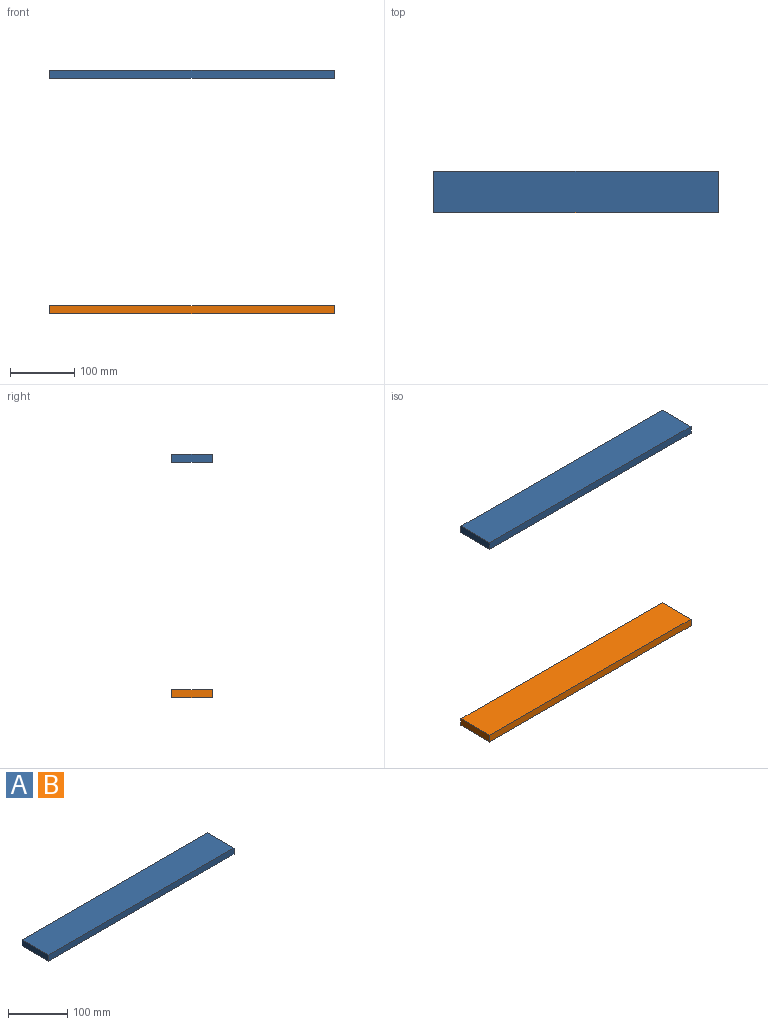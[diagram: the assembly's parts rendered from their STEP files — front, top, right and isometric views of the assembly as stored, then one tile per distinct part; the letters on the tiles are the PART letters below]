
ASSEMBLY  parts=2 mates=1
PART A: 6 faces, bbox 444.5x63.5x12.7 mm
  f0: plane 63.5x12.7mm, normal (1,0,0), area 806.5mm2, adj f1,f3,f4,f5
  f1: plane 444.5x12.7mm, normal (0,1,0), area 5645.2mm2, adj f0,f2,f4,f5
  f2: plane 63.5x12.7mm, normal (-1,0,0), area 806.5mm2, adj f1,f3,f4,f5
  f3: plane 444.5x12.7mm, normal (0,-1,0), area 5645.2mm2, adj f0,f2,f4,f5
  f4: plane 444.5x63.5mm, normal (0,0,1), area 28225.8mm2, adj f0,f1,f2,f3
  f5: plane 444.5x63.5mm, normal (0,0,-1), area 28225.8mm2, adj f0,f1,f2,f3
PART B: same geometry as A
PLACE A t=(-93.65,24.27,10.36)mm
PLACE B t=(-93.65,24.27,-357.94)mm
MATE parallel A.f4 <-> B.f5  axis (0,0,1) through (1.28,20.34,23.06)mm
